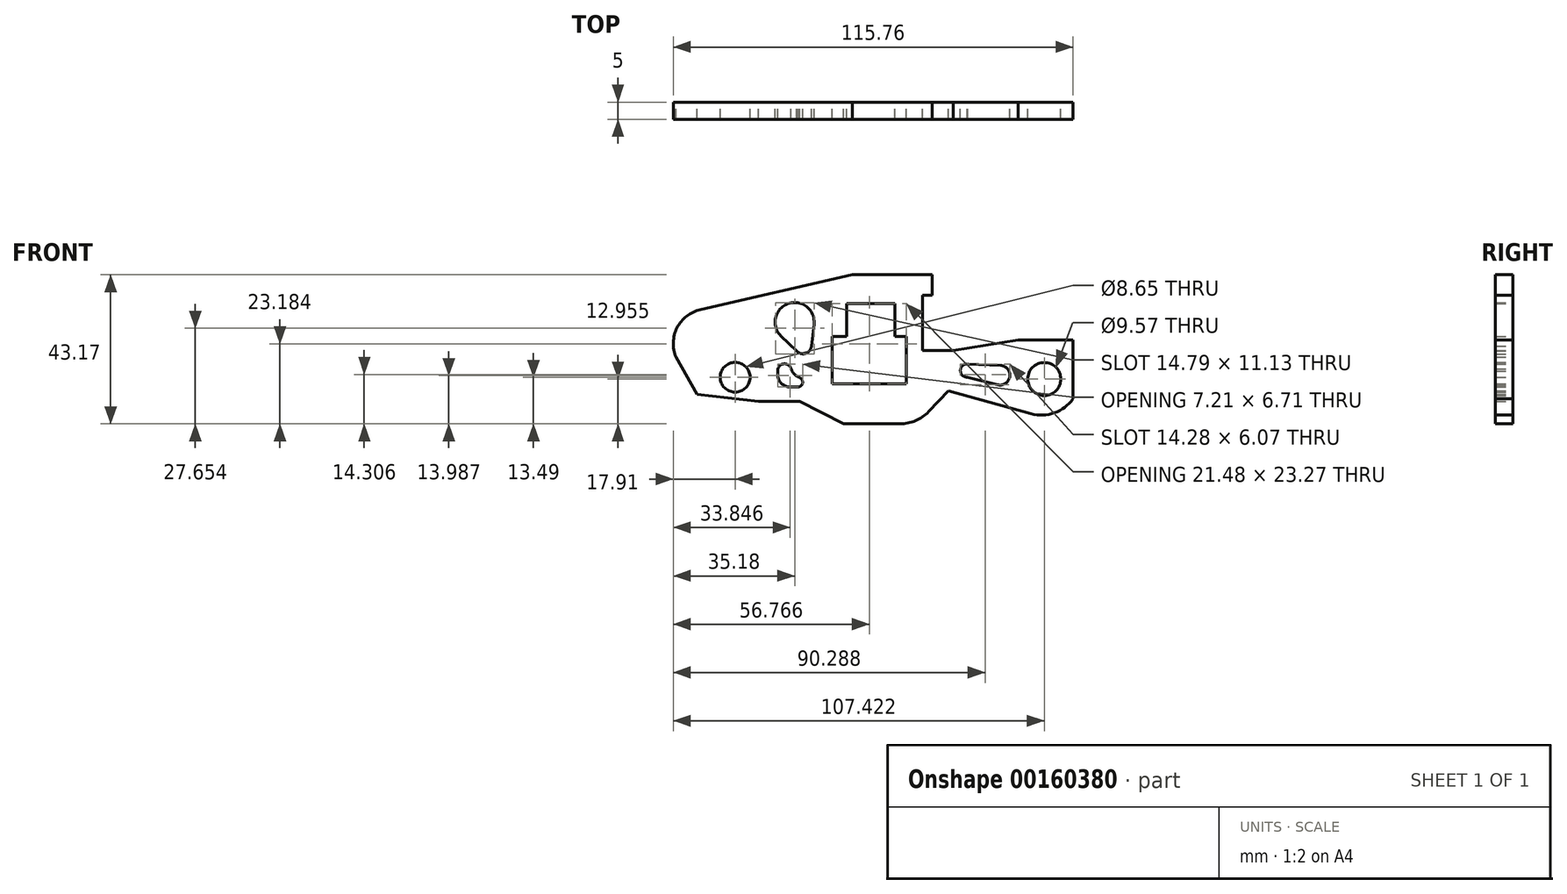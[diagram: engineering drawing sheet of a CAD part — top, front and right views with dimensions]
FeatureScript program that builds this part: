
annotation { "Feature Type Name" : "Feature", "Feature Type Description" : "" }
export const myFeature = defineFeature(function(context is Context, id is Id, definition is map)
    precondition{}
    {
        {
            var Q0;
            Q0=qCreatedBy(makeId("Front.planeOp"),FACE);
            var sketch = newSketch(context, id + "F0", { "sketchPlane" : qUnion([Q0])});
            skLineSegment(sketch, "E0", {"start": v(-126.7, 41.3) * mm, "end": v(-120.68, 30.58) * mm});
            skLineSegment(sketch, "E1", {"start": v(-120.68, 30.58) * mm, "end": v(-102.79, 28.54) * mm});
            skLineSegment(sketch, "E2", {"start": v(-102.79, 28.54) * mm, "end": v(-90.92, 28.54) * mm});
            skLineSegment(sketch, "E3", {"start": v(-90.92, 28.54) * mm, "end": v(-78.17, 21.99) * mm});
            skLineSegment(sketch, "E4", {"start": v(-78.17, 21.99) * mm, "end": v(-61.87, 21.99) * mm});
            skArc(sketch, "E5", {"start": v(-61.87, 21.99) * mm, "mid": v(-57.35, 22.9) * mm, "end": v(-53.55, 25.53) * mm});
            skLineSegment(sketch, "E6", {"start": v(-53.55, 25.53) * mm, "end": v(-47.81, 31.49) * mm});
            skLineSegment(sketch, "E7", {"start": v(-47.81, 31.49) * mm, "end": v(-23.97, 24.9) * mm});
            skArc(sketch, "E8", {"start": v(-23.97, 24.9) * mm, "mid": v(-17.18, 25.15) * mm, "end": v(-11.75, 29.25) * mm});
            skLineSegment(sketch, "E9", {"start": v(-11.75, 29.25) * mm, "end": v(-11.75, 46.25) * mm});
            skLineSegment(sketch, "E10", {"start": v(-11.75, 46.25) * mm, "end": v(-27.69, 46.25) * mm});
            skLineSegment(sketch, "E11", {"start": v(-27.69, 46.25) * mm, "end": v(-46.46, 43.24) * mm});
            skLineSegment(sketch, "E12", {"start": v(-46.46, 43.24) * mm, "end": v(-55.32, 43.24) * mm});
            skLineSegment(sketch, "E13", {"start": v(-55.32, 43.24) * mm, "end": v(-55.32, 59.27) * mm});
            skLineSegment(sketch, "E14", {"start": v(-55.32, 59.27) * mm, "end": v(-52.51, 59.27) * mm});
            skLineSegment(sketch, "E15", {"start": v(-52.51, 59.27) * mm, "end": v(-52.51, 65.16) * mm});
            skLineSegment(sketch, "E16", {"start": v(-52.51, 65.16) * mm, "end": v(-75.68, 65.16) * mm});
            skLineSegment(sketch, "E17", {"start": v(-75.68, 65.16) * mm, "end": v(-119.7, 55.05) * mm});
            skArc(sketch, "E18", {"start": v(-119.7, 55.05) * mm, "mid": v(-126.42, 49.8) * mm, "end": v(-126.7, 41.3) * mm});
            skCircle(sketch, "E19", {"center": v(-109.6, 35.48) * mm, "radius": 4.32 * mm});
            skCircle(sketch, "E20", {"center": v(-20.09, 34.94) * mm, "radius": 4.79 * mm});
            skCircle(sketch, "E21", {"center": v(-32.9, 36.06) * mm, "radius": 2.85 * mm});
            skCircle(sketch, "E22", {"center": v(-42.43, 37.4) * mm, "radius": 1.94 * mm});
            skLineSegment(sketch, "E23", {"start": v(-42.43, 39.34) * mm, "end": v(-32.77, 38.9) * mm});
            skLineSegment(sketch, "E24", {"start": v(-42.43, 35.47) * mm, "end": v(-33.57, 33.3) * mm});
            skCircle(sketch, "E25", {"center": v(-92.38, 51.47) * mm, "radius": 5.65 * mm});
            skCircle(sketch, "E26", {"center": v(-89.98, 44.74) * mm, "radius": 2.49 * mm});
            skLineSegment(sketch, "E27", {"start": v(-87.53, 44.36) * mm, "end": v(-86.77, 50.8) * mm});
            skLineSegment(sketch, "E28", {"start": v(-91.84, 43.08) * mm, "end": v(-96.3, 47.4) * mm});
            skCircle(sketch, "E29", {"center": v(-95.3, 37.39) * mm, "radius": 1.98 * mm});
            skCircle(sketch, "E30", {"center": v(-91.48, 34.06) * mm, "radius": 1.44 * mm});
            skArc(sketch, "E31", {"start": v(-93.46, 38.1) * mm, "mid": v(-92.57, 36.52) * mm, "end": v(-91.1, 35.45) * mm});
            skLineSegment(sketch, "E32", {"start": v(-91.51, 32.62) * mm, "end": v(-93.58, 32.62) * mm});
            skLineSegment(sketch, "E33", {"start": v(-97.27, 37.58) * mm, "end": v(-97.27, 36.3) * mm});
            skArc(sketch, "E34", {"start": v(-93.58, 32.62) * mm, "mid": v(-96.2, 33.7) * mm, "end": v(-97.27, 36.3) * mm});
            skLineSegment(sketch, "E35.bottom", {"start": v(-77.33, 56.8) * mm, "end": v(-63.37, 56.8) * mm});
            skLineSegment(sketch, "E35.top", {"start": v(-77.33, 47.33) * mm, "end": v(-63.37, 47.33) * mm});
            skLineSegment(sketch, "E35.left", {"start": v(-77.33, 56.8) * mm, "end": v(-77.33, 47.33) * mm});
            skLineSegment(sketch, "E35.right", {"start": v(-63.37, 56.8) * mm, "end": v(-63.37, 47.33) * mm});
            skLineSegment(sketch, "E36.bottom", {"start": v(-81.49, 47.33) * mm, "end": v(-60, 47.33) * mm});
            skLineSegment(sketch, "E36.top", {"start": v(-81.49, 33.54) * mm, "end": v(-60, 33.54) * mm});
            skLineSegment(sketch, "E36.left", {"start": v(-81.49, 47.33) * mm, "end": v(-81.49, 33.54) * mm});
            skLineSegment(sketch, "E36.right", {"start": v(-60, 47.33) * mm, "end": v(-60, 33.54) * mm});
            skSolve(sketch);
        }
        {
            var Q0;
            Q0 = qSketchRegion(id + "F0", true);
            extrude(context, id + "F1", {"entities" : qUnion([Q0]), "depth" : 5 * mm});
        }
    });
